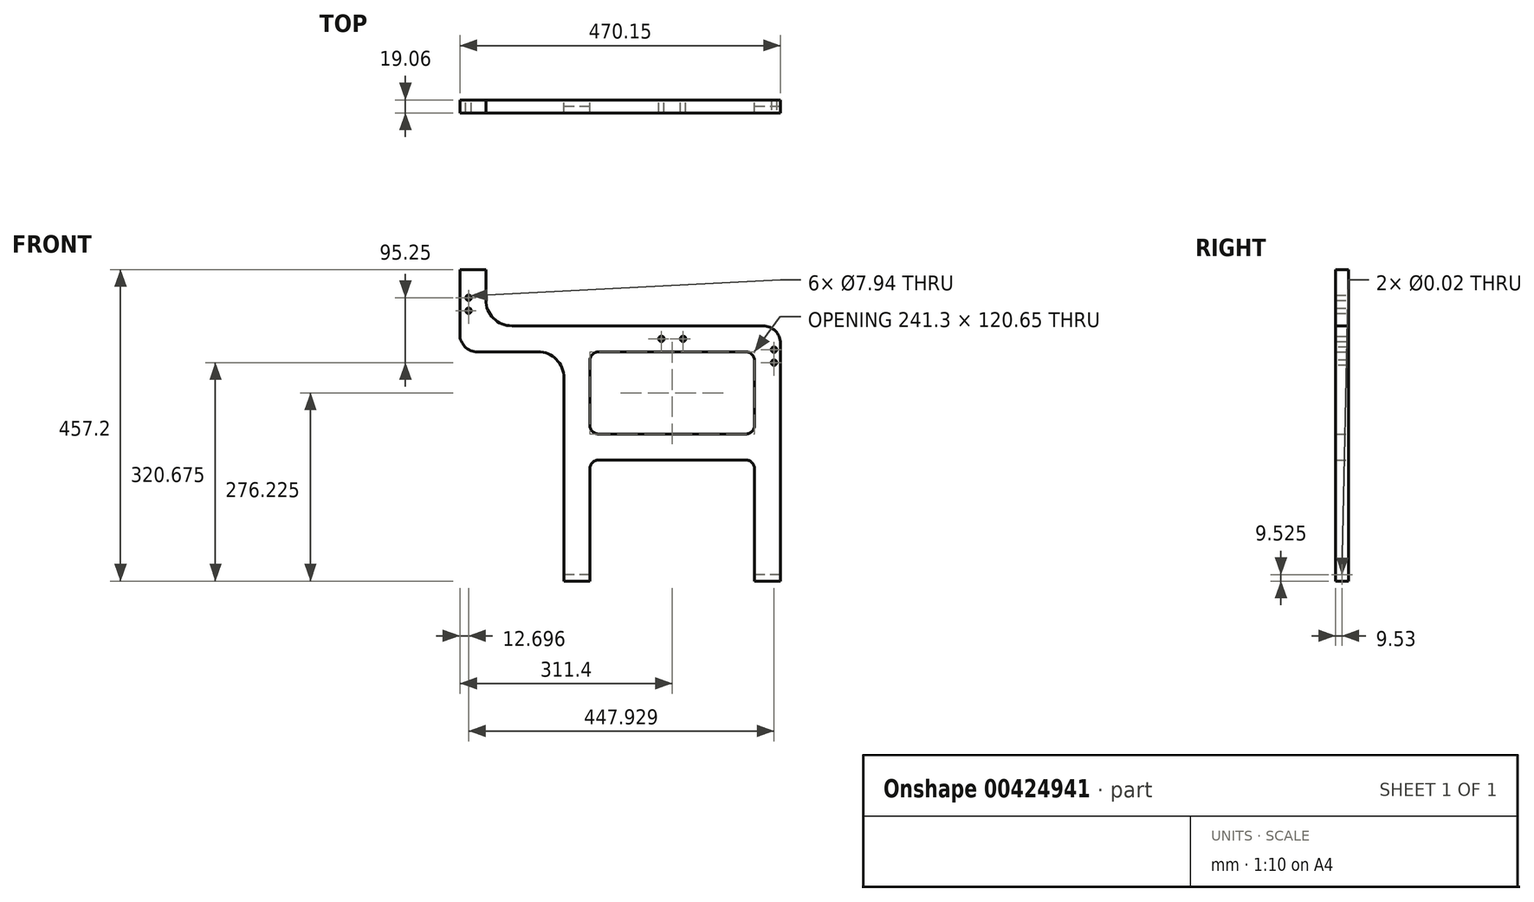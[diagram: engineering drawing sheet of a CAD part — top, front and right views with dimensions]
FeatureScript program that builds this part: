
annotation { "Feature Type Name" : "Feature", "Feature Type Description" : "" }
export const myFeature = defineFeature(function(context is Context, id is Id, definition is map)
    precondition{}
    {
        {
            var Q0;
            Q0=qCreatedBy(makeId("Front.planeOp"),FACE);
            var sketch = newSketch(context, id + "F0", { "sketchPlane" : qUnion([Q0])});
            skLineSegment(sketch, "E0", {"start": v(0, 0) * mm, "end": v(-38.1, 0) * mm});
            skLineSegment(sketch, "E1", {"start": v(-38.1, 0) * mm, "end": v(-38.1, 177.8) * mm});
            skLineSegment(sketch, "E2", {"start": v(-38.1, 177.8) * mm, "end": v(-279.4, 177.8) * mm});
            skLineSegment(sketch, "E3", {"start": v(-279.4, 177.8) * mm, "end": v(-279.4, 0) * mm});
            skLineSegment(sketch, "E4", {"start": v(-279.4, 0) * mm, "end": v(-317.5, 0) * mm});
            skLineSegment(sketch, "E5", {"start": v(-317.5, 0) * mm, "end": v(-317.5, 336.55) * mm});
            skLineSegment(sketch, "E6", {"start": v(-317.5, 336.55) * mm, "end": v(-470.15, 336.55) * mm});
            skLineSegment(sketch, "E7", {"start": v(-470.15, 336.55) * mm, "end": v(-470.15, 457.2) * mm});
            skLineSegment(sketch, "E8", {"start": v(-470.15, 457.2) * mm, "end": v(-432.05, 457.2) * mm});
            skLineSegment(sketch, "E9", {"start": v(-432.05, 457.2) * mm, "end": v(-432.05, 374.65) * mm});
            skLineSegment(sketch, "E10", {"start": v(-432.05, 374.65) * mm, "end": v(0, 374.65) * mm});
            skLineSegment(sketch, "E11", {"start": v(0, 374.65) * mm, "end": v(0, 0) * mm});
            skLineSegment(sketch, "E12", {"start": v(-279.4, 336.55) * mm, "end": v(-279.4, 215.9) * mm});
            skLineSegment(sketch, "E13", {"start": v(-279.4, 215.9) * mm, "end": v(-38.1, 215.9) * mm});
            skLineSegment(sketch, "E14", {"start": v(-38.1, 215.9) * mm, "end": v(-38.1, 336.55) * mm});
            skLineSegment(sketch, "E15", {"start": v(-38.1, 336.55) * mm, "end": v(-279.4, 336.55) * mm});
            skPoint(sketch, "E16.visualSharp", {"position": v(-432.05, 374.65) * mm});
            skSolve(sketch);
        }
        {
            var Q0;
            Q0=makeQuery(id+"F0.imprint","IMPRINT",FACE,{"disambiguationData":[TD([[makeQuery(id+"F0.imprint","IMPRINT",EDGE,{"derivedFrom":sQuery(id+"F0.wireOp",EDGE,"E0")}),-1.0]])]});
            extrude(context, id + "F1", {"entities" : qUnion([Q0]), "depth" : 19.05 * mm, "symmetric" : true});
        }
        {
            var Q0;
            Q0=makeQuery(id+"F1.opExtrude","SWEPT_EDGE",EDGE,{"disambiguationData":[OSD([sQuery(id+"F0.wireOp",EDGE,"E12"),sQuery(id+"F0.wireOp",EDGE,"E15")])]});
            var Q1;
            Q1=makeQuery(id+"F1.opExtrude","SWEPT_EDGE",EDGE,{"disambiguationData":[OSD([sQuery(id+"F0.wireOp",EDGE,"E12"),sQuery(id+"F0.wireOp",EDGE,"E13")])]});
            var Q2;
            Q2=makeQuery(id+"F1.opExtrude","SWEPT_EDGE",EDGE,{"disambiguationData":[OSD([sQuery(id+"F0.wireOp",EDGE,"E13"),sQuery(id+"F0.wireOp",EDGE,"E14")])]});
            var Q3;
            Q3=makeQuery(id+"F1.opExtrude","SWEPT_EDGE",EDGE,{"disambiguationData":[OSD([sQuery(id+"F0.wireOp",EDGE,"E14"),sQuery(id+"F0.wireOp",EDGE,"E15")])]});
            var Q4;
            Q4=makeQuery(id+"F1.opExtrude","SWEPT_EDGE",EDGE,{"disambiguationData":[OSD([sQuery(id+"F0.wireOp",EDGE,"E2"),sQuery(id+"F0.wireOp",EDGE,"E3")])]});
            var Q5;
            Q5=makeQuery(id+"F1.opExtrude","SWEPT_EDGE",EDGE,{"disambiguationData":[OSD([sQuery(id+"F0.wireOp",EDGE,"E1"),sQuery(id+"F0.wireOp",EDGE,"E2")])]});
            fillet(context, id + "F2", {"entities" : qUnion([Q0, Q1, Q2, Q3, Q4, Q5]), "radius" : 12.7 * mm, "tangentPropagation" : true, "allowEdgeOverflow" : false});
        }
        {
            var Q0;
            Q0=makeQuery(id+"F1.opExtrude","SWEPT_EDGE",EDGE,{"disambiguationData":[OSD([sQuery(id+"F0.wireOp",EDGE,"E5"),sQuery(id+"F0.wireOp",EDGE,"E6")])]});
            var Q1;
            Q1=makeQuery(id+"F1.opExtrude","SWEPT_EDGE",EDGE,{"disambiguationData":[OSD([sQuery(id+"F0.wireOp",EDGE,"E9"),sQuery(id+"F0.wireOp",EDGE,"E10")])]});
            fillet(context, id + "F3", {"entities" : qUnion([Q0, Q1]), "radius" : 38.1 * mm, "tangentPropagation" : true, "allowEdgeOverflow" : false});
        }
        {
            var Q0;
            Q0=makeQuery(id+"F1.opExtrude","SWEPT_FACE",FACE,{"disambiguationData":[OSD([sQuery(id+"F0.wireOp",EDGE,"E11")])]});
            var sketch = newSketch(context, id + "F4", { "sketchPlane" : qUnion([Q0])});
            skPoint(sketch, "E17", {"position": v(0, 9.53) * mm});
            skSolve(sketch);
        }
        {
            var Q0;
            Q0=sQuery(id+"F4.wireOp",VERTEX,"E17");
            var Q1;
            Q1=makeQuery(id+"F1.opExtrude","SWEPT_BODY",BODY,{"disambiguationData":[OSD([sQuery(id+"F0.wireOp",EDGE,"E0"),sQuery(id+"F0.wireOp",EDGE,"E1"),sQuery(id+"F0.wireOp",EDGE,"E2"),sQuery(id+"F0.wireOp",EDGE,"E3"),sQuery(id+"F0.wireOp",EDGE,"E4"),sQuery(id+"F0.wireOp",EDGE,"E5"),sQuery(id+"F0.wireOp",EDGE,"E6"),sQuery(id+"F0.wireOp",EDGE,"E7"),sQuery(id+"F0.wireOp",EDGE,"E8"),sQuery(id+"F0.wireOp",EDGE,"E9"),sQuery(id+"F0.wireOp",EDGE,"E10"),sQuery(id+"F0.wireOp",EDGE,"E11"),sQuery(id+"F0.wireOp",EDGE,"E12"),sQuery(id+"F0.wireOp",EDGE,"E13"),sQuery(id+"F0.wireOp",EDGE,"E14"),sQuery(id+"F0.wireOp",EDGE,"E15")])]});
            hole(context, id + "F5", {"style" : HoleStyle.SIMPLE, "endStyle" : HoleEndStyle.THROUGH, "standardTappedOrClearance" : lookupTablePath({ "standard" : "ANSI", "size" : "1/2 (0.5)", "type" : "Drilled" }), "standardBlindInLast" : lookupTablePath({ "standard" : "ANSI", "size" : "1/2", "type" : "Drilled" }), "holeDiameter" : 1 / 50.8 * mm, "isTappedThrough" : true, "tappedDepth" : 29.3 * mm, "tapClearance" : 3, "locations" : qUnion([Q0]), "scope" : qUnion([Q1]), "startStyle" : HoleStartStyle.SKETCH});
        }
        {
            var Q0;
            Q0=makeQuery(id+"F1.opExtrude","SWEPT_EDGE",EDGE,{"disambiguationData":[OSD([sQuery(id+"F0.wireOp",EDGE,"E6"),sQuery(id+"F0.wireOp",EDGE,"E7")])]});
            var Q1;
            Q1=makeQuery(id+"F1.opExtrude","SWEPT_EDGE",EDGE,{"disambiguationData":[OSD([sQuery(id+"F0.wireOp",EDGE,"E10"),sQuery(id+"F0.wireOp",EDGE,"E11")])]});
            fillet(context, id + "F6", {"entities" : qUnion([Q0, Q1]), "radius" : 25.4 * mm, "tangentPropagation" : true, "allowEdgeOverflow" : false});
        }
        {
            var Q0;
            Q0=makeQuery(id+"F1.opExtrude","CAP_FACE",FACE,{"disambiguationData":[OSD([sQuery(id+"F0.wireOp",EDGE,"E0"),sQuery(id+"F0.wireOp",EDGE,"E1"),sQuery(id+"F0.wireOp",EDGE,"E2"),sQuery(id+"F0.wireOp",EDGE,"E3"),sQuery(id+"F0.wireOp",EDGE,"E4"),sQuery(id+"F0.wireOp",EDGE,"E5"),sQuery(id+"F0.wireOp",EDGE,"E6"),sQuery(id+"F0.wireOp",EDGE,"E7"),sQuery(id+"F0.wireOp",EDGE,"E8"),sQuery(id+"F0.wireOp",EDGE,"E9"),sQuery(id+"F0.wireOp",EDGE,"E10"),sQuery(id+"F0.wireOp",EDGE,"E11"),sQuery(id+"F0.wireOp",EDGE,"E12"),sQuery(id+"F0.wireOp",EDGE,"E13"),sQuery(id+"F0.wireOp",EDGE,"E14"),sQuery(id+"F0.wireOp",EDGE,"E15")])],"isStart":false});
            var sketch = newSketch(context, id + "F7", { "sketchPlane" : qUnion([Q0])});
            skPoint(sketch, "E18", {"position": v(-174.62, 355.6) * mm});
            skPoint(sketch, "E19", {"position": v(-142.88, 355.6) * mm});
            skSolve(sketch);
        }
        {
            var Q0;
            Q0=sQuery(id+"F7.wireOp",VERTEX,"E18");
            var Q1;
            Q1=sQuery(id+"F7.wireOp",VERTEX,"E19");
            var Q2;
            Q2=makeQuery(id+"F1.opExtrude","SWEPT_BODY",BODY,{"disambiguationData":[OSD([sQuery(id+"F0.wireOp",EDGE,"E0"),sQuery(id+"F0.wireOp",EDGE,"E1"),sQuery(id+"F0.wireOp",EDGE,"E2"),sQuery(id+"F0.wireOp",EDGE,"E3"),sQuery(id+"F0.wireOp",EDGE,"E4"),sQuery(id+"F0.wireOp",EDGE,"E5"),sQuery(id+"F0.wireOp",EDGE,"E6"),sQuery(id+"F0.wireOp",EDGE,"E7"),sQuery(id+"F0.wireOp",EDGE,"E8"),sQuery(id+"F0.wireOp",EDGE,"E9"),sQuery(id+"F0.wireOp",EDGE,"E10"),sQuery(id+"F0.wireOp",EDGE,"E11"),sQuery(id+"F0.wireOp",EDGE,"E12"),sQuery(id+"F0.wireOp",EDGE,"E13"),sQuery(id+"F0.wireOp",EDGE,"E14"),sQuery(id+"F0.wireOp",EDGE,"E15")])]});
            hole(context, id + "F8", {"style" : HoleStyle.SIMPLE, "endStyle" : HoleEndStyle.THROUGH, "standardTappedOrClearance" : lookupTablePath({ "standard" : "ANSI", "engagement" : "75%", "pitch" : "16 tpi", "size" : "3/8", "type" : "Tapped" }), "standardBlindInLast" : lookupTablePath({ "standard" : "ANSI", "engagement" : "75%", "pitch" : "16 tpi", "size" : "3/8", "type" : "Tapped" }), "holeDiameter" : 7.94 * mm, "showTappedDepth" : true, "isTappedThrough" : true, "tappedDepth" : 29.3 * mm, "tapClearance" : 3, "locations" : qUnion([Q0, Q1]), "scope" : qUnion([Q2]), "majorDiameter" : 9.53 * mm, "startStyle" : HoleStartStyle.SKETCH});
        }
        {
            var Q0;
            Q0=makeQuery(id+"F1.opExtrude","CAP_FACE",FACE,{"disambiguationData":[OSD([sQuery(id+"F0.wireOp",EDGE,"E0"),sQuery(id+"F0.wireOp",EDGE,"E1"),sQuery(id+"F0.wireOp",EDGE,"E2"),sQuery(id+"F0.wireOp",EDGE,"E3"),sQuery(id+"F0.wireOp",EDGE,"E4"),sQuery(id+"F0.wireOp",EDGE,"E5"),sQuery(id+"F0.wireOp",EDGE,"E6"),sQuery(id+"F0.wireOp",EDGE,"E7"),sQuery(id+"F0.wireOp",EDGE,"E8"),sQuery(id+"F0.wireOp",EDGE,"E9"),sQuery(id+"F0.wireOp",EDGE,"E10"),sQuery(id+"F0.wireOp",EDGE,"E11"),sQuery(id+"F0.wireOp",EDGE,"E12"),sQuery(id+"F0.wireOp",EDGE,"E13"),sQuery(id+"F0.wireOp",EDGE,"E14"),sQuery(id+"F0.wireOp",EDGE,"E15")])],"isStart":true});
            var sketch = newSketch(context, id + "F9", { "sketchPlane" : qUnion([Q0])});
            skLineSegment(sketch, "E20", {"start": v(9.52, 339.73) * mm, "end": v(9.53, 320.68) * mm, "construction": true});
            skSolve(sketch);
        }
        {
            var Q0;
            Q0=sQuery(id+"F9.wireOp",VERTEX,"E20.end");
            var Q1;
            Q1=sQuery(id+"F9.wireOp",VERTEX,"E20.start");
            var Q2;
            Q2=makeQuery(id+"F1.opExtrude","SWEPT_BODY",BODY,{"disambiguationData":[OSD([sQuery(id+"F0.wireOp",EDGE,"E0"),sQuery(id+"F0.wireOp",EDGE,"E1"),sQuery(id+"F0.wireOp",EDGE,"E2"),sQuery(id+"F0.wireOp",EDGE,"E3"),sQuery(id+"F0.wireOp",EDGE,"E4"),sQuery(id+"F0.wireOp",EDGE,"E5"),sQuery(id+"F0.wireOp",EDGE,"E6"),sQuery(id+"F0.wireOp",EDGE,"E7"),sQuery(id+"F0.wireOp",EDGE,"E8"),sQuery(id+"F0.wireOp",EDGE,"E9"),sQuery(id+"F0.wireOp",EDGE,"E10"),sQuery(id+"F0.wireOp",EDGE,"E11"),sQuery(id+"F0.wireOp",EDGE,"E12"),sQuery(id+"F0.wireOp",EDGE,"E13"),sQuery(id+"F0.wireOp",EDGE,"E14"),sQuery(id+"F0.wireOp",EDGE,"E15")])]});
            hole(context, id + "F10", {"style" : HoleStyle.SIMPLE, "endStyle" : HoleEndStyle.THROUGH, "standardTappedOrClearance" : lookupTablePath({ "standard" : "ANSI", "engagement" : "75%", "pitch" : "16 tpi", "size" : "3/8", "type" : "Tapped" }), "standardBlindInLast" : lookupTablePath({ "standard" : "ANSI", "engagement" : "75%", "pitch" : "16 tpi", "size" : "3/8", "type" : "Tapped" }), "holeDiameter" : 7.94 * mm, "showTappedDepth" : true, "isTappedThrough" : true, "tappedDepth" : 29.3 * mm, "tapClearance" : 3, "locations" : qUnion([Q0, Q1]), "scope" : qUnion([Q2]), "majorDiameter" : 9.53 * mm, "startStyle" : HoleStartStyle.SKETCH});
        }
        {
            var Q0;
            Q0=makeQuery(id+"F1.opExtrude","CAP_FACE",FACE,{"disambiguationData":[OSD([sQuery(id+"F0.wireOp",EDGE,"E0"),sQuery(id+"F0.wireOp",EDGE,"E1"),sQuery(id+"F0.wireOp",EDGE,"E2"),sQuery(id+"F0.wireOp",EDGE,"E3"),sQuery(id+"F0.wireOp",EDGE,"E4"),sQuery(id+"F0.wireOp",EDGE,"E5"),sQuery(id+"F0.wireOp",EDGE,"E6"),sQuery(id+"F0.wireOp",EDGE,"E7"),sQuery(id+"F0.wireOp",EDGE,"E8"),sQuery(id+"F0.wireOp",EDGE,"E9"),sQuery(id+"F0.wireOp",EDGE,"E10"),sQuery(id+"F0.wireOp",EDGE,"E11"),sQuery(id+"F0.wireOp",EDGE,"E12"),sQuery(id+"F0.wireOp",EDGE,"E13"),sQuery(id+"F0.wireOp",EDGE,"E14"),sQuery(id+"F0.wireOp",EDGE,"E15")])],"isStart":false});
            var sketch = newSketch(context, id + "F11", { "sketchPlane" : qUnion([Q0])});
            skLineSegment(sketch, "E21", {"start": v(-457.45, 415.93) * mm, "end": v(-457.45, 396.88) * mm, "construction": true});
            skSolve(sketch);
        }
        {
            var Q0;
            Q0=sQuery(id+"F11.wireOp",VERTEX,"E21.start");
            var Q1;
            Q1=sQuery(id+"F11.wireOp",VERTEX,"E21.end");
            var Q2;
            Q2=makeQuery(id+"F1.opExtrude","SWEPT_BODY",BODY,{"disambiguationData":[OSD([sQuery(id+"F0.wireOp",EDGE,"E0"),sQuery(id+"F0.wireOp",EDGE,"E1"),sQuery(id+"F0.wireOp",EDGE,"E2"),sQuery(id+"F0.wireOp",EDGE,"E3"),sQuery(id+"F0.wireOp",EDGE,"E4"),sQuery(id+"F0.wireOp",EDGE,"E5"),sQuery(id+"F0.wireOp",EDGE,"E6"),sQuery(id+"F0.wireOp",EDGE,"E7"),sQuery(id+"F0.wireOp",EDGE,"E8"),sQuery(id+"F0.wireOp",EDGE,"E9"),sQuery(id+"F0.wireOp",EDGE,"E10"),sQuery(id+"F0.wireOp",EDGE,"E11"),sQuery(id+"F0.wireOp",EDGE,"E12"),sQuery(id+"F0.wireOp",EDGE,"E13"),sQuery(id+"F0.wireOp",EDGE,"E14"),sQuery(id+"F0.wireOp",EDGE,"E15")])]});
            hole(context, id + "F12", {"style" : HoleStyle.SIMPLE, "endStyle" : HoleEndStyle.THROUGH, "standardTappedOrClearance" : lookupTablePath({ "standard" : "ANSI", "engagement" : "75%", "pitch" : "16 tpi", "size" : "3/8", "type" : "Tapped" }), "standardBlindInLast" : lookupTablePath({ "standard" : "ANSI", "engagement" : "75%", "pitch" : "16 tpi", "size" : "3/8", "type" : "Tapped" }), "holeDiameter" : 7.94 * mm, "showTappedDepth" : true, "isTappedThrough" : true, "tappedDepth" : 22.24 * mm, "tapClearance" : 3, "locations" : qUnion([Q0, Q1]), "scope" : qUnion([Q2]), "majorDiameter" : 9.53 * mm, "startStyle" : HoleStartStyle.SKETCH});
        }
    });
